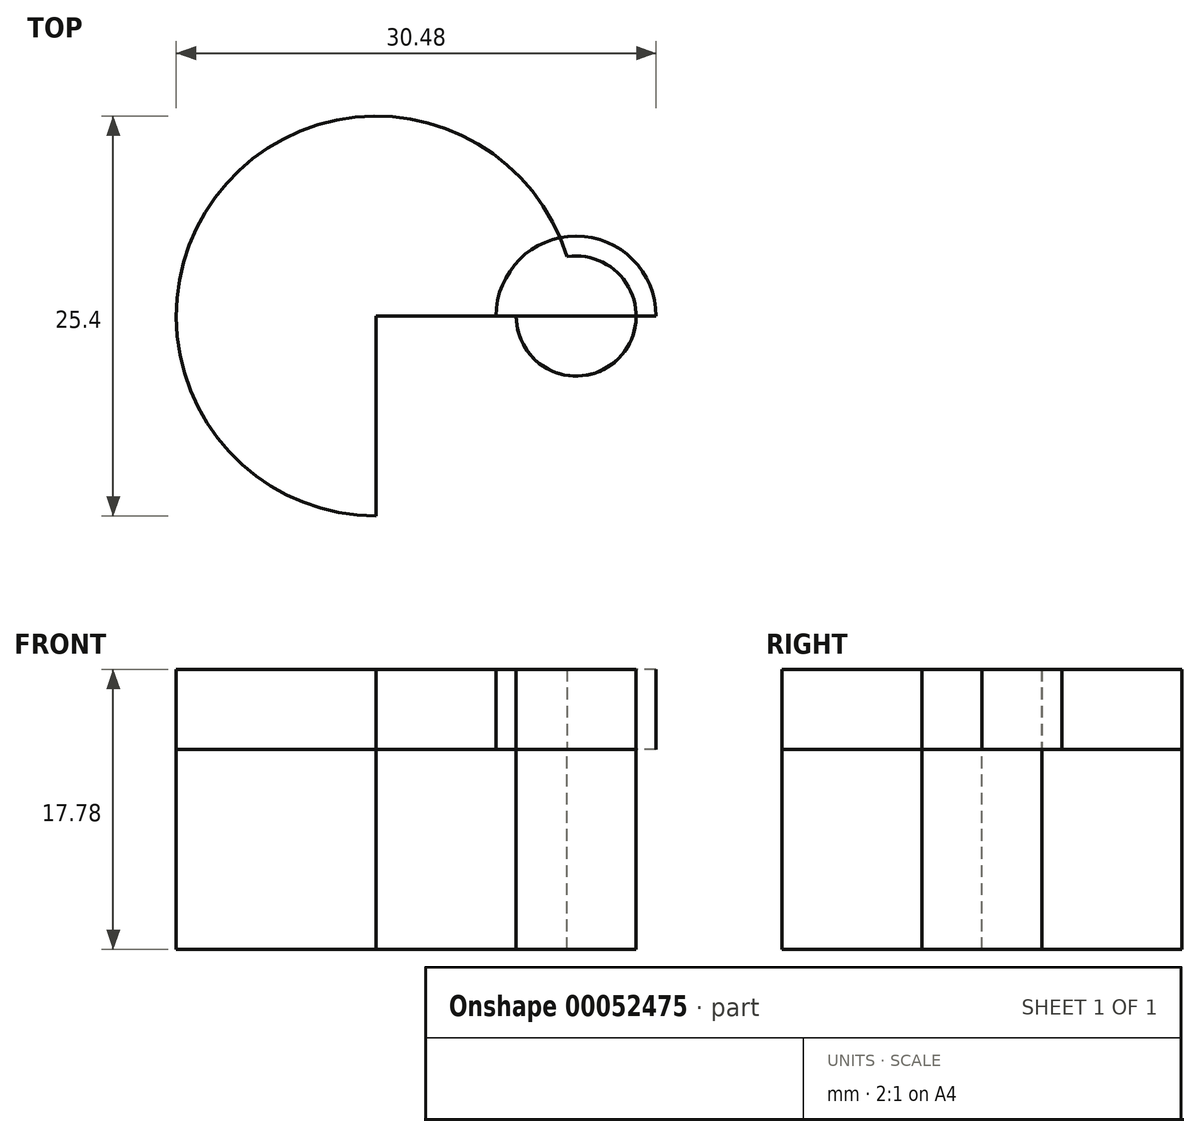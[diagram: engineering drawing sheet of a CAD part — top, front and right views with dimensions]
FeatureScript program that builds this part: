
annotation { "Feature Type Name" : "Feature", "Feature Type Description" : "" }
export const myFeature = defineFeature(function(context is Context, id is Id, definition is map)
    precondition{}
    {
        {
            var Q0;
            Q0=qCreatedBy(makeId("Top.planeOp"),FACE);
            var sketch = newSketch(context, id + "F0", { "sketchPlane" : qUnion([Q0])});
            skArc(sketch, "E0", {"start": v(12.13, 3.77) * mm, "mid": v(-10.23, 7.53) * mm, "end": v(0, -12.7) * mm});
            skLineSegment(sketch, "E1.bottom", {"start": v(0, 0) * mm, "end": v(8.9, 0) * mm});
            skLineSegment(sketch, "E1.left", {"start": v(0, 0) * mm, "end": v(0, -12.7) * mm});
            skArc(sketch, "E2", {"start": v(8.9, 0) * mm, "mid": v(15.59, -2.48) * mm, "end": v(12.13, 3.77) * mm});
            skSolve(sketch);
        }
        {
            var Q0;
            Q0 = qSketchRegion(id + "F0", true);
            extrude(context, id + "F1", {"entities" : qUnion([Q0]), "depth" : 5.08 * mm});
        }
        {
            var Q0;
            Q0 = qSketchRegion(id + "F0", true);
            extrude(context, id + "F2", {"entities" : qUnion([Q0]), "oppositeDirection" : true, "depth" : 12.7 * mm});
        }
        {
            var Q0;
            Q0=qCreatedBy(makeId("Top.planeOp"),FACE);
            var sketch = newSketch(context, id + "F3", { "sketchPlane" : qUnion([Q0])});
            skArc(sketch, "E3", {"start": v(17.78, 0) * mm, "mid": v(12.7, 5.08) * mm, "end": v(7.62, 0) * mm});
            skLineSegment(sketch, "E4", {"start": v(7.62, 0) * mm, "end": v(17.78, 0) * mm});
            skSolve(sketch);
        }
        {
            var Q0;
            Q0 = qSketchRegion(id + "F3", true);
            extrude(context, id + "F4", {"entities" : qUnion([Q0]), "depth" : 5.08 * mm});
        }
    });
